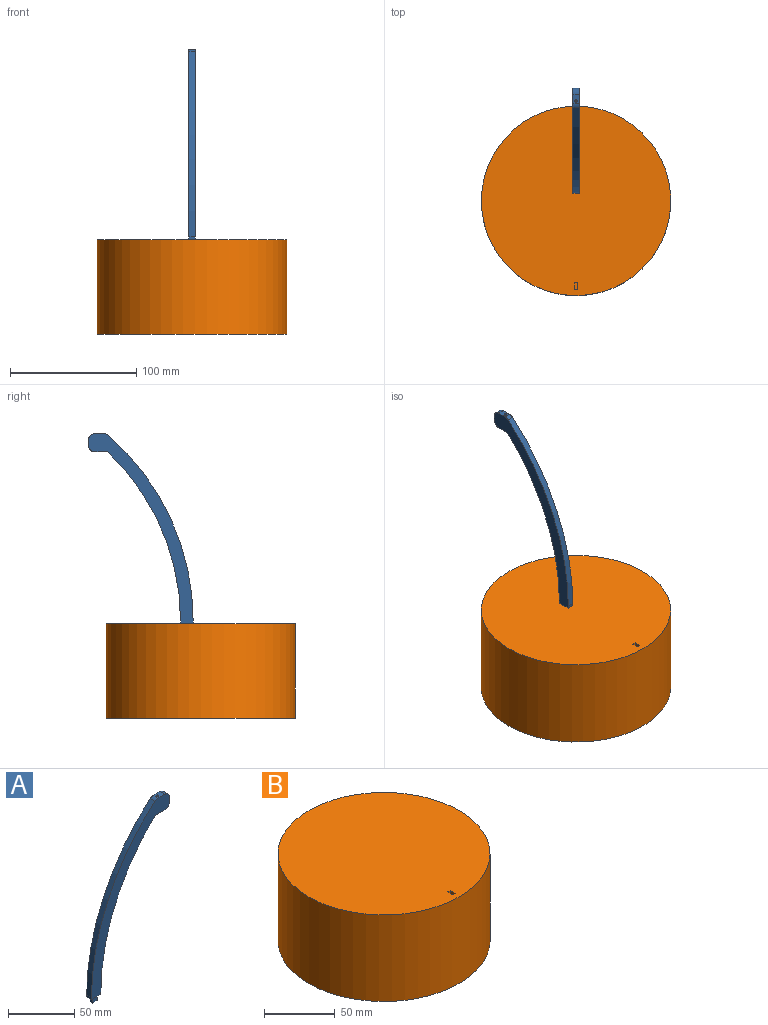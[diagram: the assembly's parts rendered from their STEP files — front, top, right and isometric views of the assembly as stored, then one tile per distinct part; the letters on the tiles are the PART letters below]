
ASSEMBLY  parts=2 mates=1
PART A: 19 faces, bbox 82.8x5x155.3 mm
  f0: plane 10x5mm, normal (0,0,-1), area 37.5mm2, adj f6,f7,f8,f9,f10,f12,f13,f14
  f1: plane 10x5mm, normal (0,0,-1), area 46.9mm2, adj f5,f6,f7,f16,f18
  f2: plane 5x4.3mm, normal (1,0,0), area 21.5mm2, adj f6,f7,f16,f17
  f3: plane 7.15x5mm, normal (0,0,1), area 32.6mm2, adj f6,f7,f15,f17,f18
  f4: cylinder r=194.1mm len=147.06mm, axis (0,1,0), area 834.3mm2, adj f6,f7,f9,f15
  f5: cylinder r=184.1mm len=133.97mm, axis (0,1,0), area 750.2mm2, adj f1,f6,f7,f8
  f6: plane 150.27x82.84mm, normal (0,-1,0), area 1810.6mm2, adj f0,f1,f2,f3,f4,f5,f8,f9
  f7: plane 150.27x82.84mm, normal (0,1,0), area 1810.6mm2, adj f0,f1,f2,f3,f4,f5,f8,f9
  f8: plane 5x2mm, normal (1,0,0), area 10mm2, adj f0,f5,f6,f7
  f9: plane 5x2mm, normal (-1,0,0), area 10mm2, adj f0,f4,f6,f7
  f10: plane 5x2.5mm, normal (-1,0,0), area 12.5mm2, adj f0,f11,f13,f14
  f11: plane 5x2.5mm, normal (0,0,-1), area 12.5mm2, adj f10,f12,f13,f14
  f12: plane 5x2.5mm, normal (1,0,0), area 12.5mm2, adj f0,f11,f13,f14
  f13: plane 5x5mm, normal (0,-1,0), area 25mm2, adj f0,f10,f11,f12
  f14: plane 5x5mm, normal (0,1,0), area 25mm2, adj f0,f10,f11,f12
  f15: cylinder r=5mm len=5mm, axis (0,1,0), area 17.8mm2, adj f3,f4,f6,f7
  f16: cylinder r=5mm len=5mm, axis (0,1,0), area 39.3mm2, adj f1,f2,f6,f7
  f17: cylinder r=5mm len=5mm, axis (0,-1,0), area 39.3mm2, adj f2,f3,f6,f7
  f18: cylinder r=1mm len=14.3mm, axis (0,0,-1), area 89.8mm2, adj f1,f3
PART B: 8 faces, bbox 150x150x75 mm
  f0: plane 150x150mm, normal (0,0,1), area 17659mm2, adj f2,f3,f4,f5,f6
  f1: plane 150x150mm, normal (0,0,-1), area 17671.5mm2, adj f2
  f2: cylinder r=75mm len=150mm, axis (0,0,-1), area 35342.9mm2, adj f0,f1
  f3: plane 6x2.5mm, normal (0,-1,0), area 15mm2, adj f0,f4,f6,f7
  f4: plane 6x5mm, normal (1,0,0), area 30mm2, adj f0,f3,f5,f7
  f5: plane 6x2.5mm, normal (0,1,0), area 15mm2, adj f0,f4,f6,f7
  f6: plane 6x5mm, normal (-1,0,0), area 30mm2, adj f0,f3,f5,f7
  f7: plane 5x2.5mm, normal (0,0,1), area 12.5mm2, adj f3,f4,f5,f6
PLACE A rot(axis=(0,0,1),90deg) t=(-26.49,11.24,51.74)mm
PLACE B t=(-26.49,0.2,-24.26)mm
MATE slider A.f0 <-> B.f0  axis (0,0,-1) through (-26.49,6.24,50.74)mm
